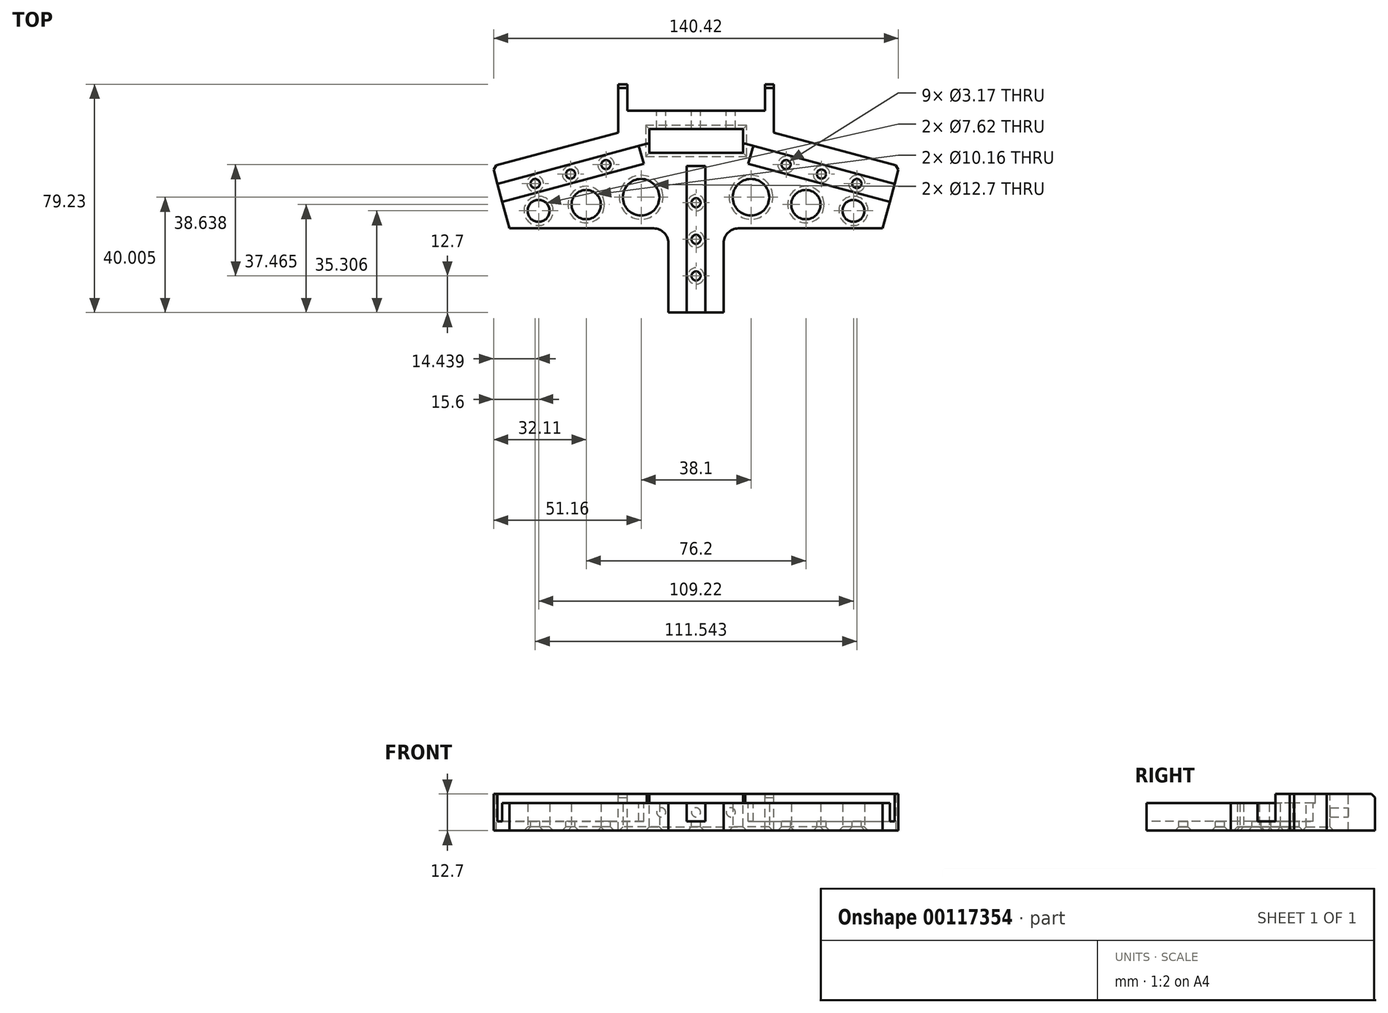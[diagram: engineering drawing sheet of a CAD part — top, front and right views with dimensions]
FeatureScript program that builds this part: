
annotation { "Feature Type Name" : "Feature", "Feature Type Description" : "" }
export const myFeature = defineFeature(function(context is Context, id is Id, definition is map)
    precondition{}
    {
        {
            var Q0;
            Q0=qCreatedBy(makeId("Top.planeOp"),FACE);
            var sketch = newSketch(context, id + "F0", { "sketchPlane" : qUnion([Q0])});
            skLineSegment(sketch, "E0", {"start": v(-70.54, 0) * mm, "end": v(70.54, 0) * mm});
            skLineSegment(sketch, "E1", {"start": v(70.54, 0) * mm, "end": v(0, 18.9) * mm});
            skLineSegment(sketch, "E2", {"start": v(0, 18.9) * mm, "end": v(-70.54, 0) * mm});
            skLineSegment(sketch, "E3", {"start": v(-70.54, 0) * mm, "end": v(-56.92, -50.8) * mm});
            skLineSegment(sketch, "E4", {"start": v(70.54, 0) * mm, "end": v(56.92, -50.8) * mm});
            skPoint(sketch, "E5.orphan", {"position": v(0, -50.8) * mm});
            skLineSegment(sketch, "E6", {"start": v(-56.92, -50.8) * mm, "end": v(56.92, -50.8) * mm});
            skSolve(sketch);
        }
        {
            var Q0;
            Q0=qSketchRegion(id+"F0",true);
            extrude(context, id + "F1", {"entities" : qUnion([Q0]), "depth" : 9.52 * mm});
        }
        {
            var Q0;
            Q0=makeQuery(id+"F1.opExtrude","CAP_FACE",FACE,{"disambiguationData":[OSD([sQuery(id+"F0.wireOp",EDGE,"E1"),sQuery(id+"F0.wireOp",EDGE,"E2"),sQuery(id+"F0.wireOp",EDGE,"E3"),sQuery(id+"F0.wireOp",EDGE,"E4"),sQuery(id+"F0.wireOp",EDGE,"E6")])],"isStart":false});
            var sketch = newSketch(context, id + "F2", { "sketchPlane" : qUnion([Q0])});
            skLineSegment(sketch, "E7", {"start": v(-70.54, 0) * mm, "end": v(0, 18.9) * mm});
            skLineSegment(sketch, "E8", {"start": v(0, 18.9) * mm, "end": v(70.54, 0) * mm});
            skLineSegment(sketch, "E9", {"start": v(70.54, 0) * mm, "end": v(68.9, -6.13) * mm});
            skLineSegment(sketch, "E10", {"start": v(68.9, -6.13) * mm, "end": v(0, 12.33) * mm});
            skLineSegment(sketch, "E11", {"start": v(0, 12.33) * mm, "end": v(-68.9, -6.13) * mm});
            skLineSegment(sketch, "E12", {"start": v(-68.9, -6.13) * mm, "end": v(-70.54, 0) * mm});
            skSolve(sketch);
        }
        {
            var Q0;
            Q0=qSketchRegion(id+"F2",true);
            extrude(context, id + "F3", {"entities" : qUnion([Q0]), "operationType" : NewBodyOperationType.ADD, "endBound" : BoundingType.SYMMETRIC, "depth" : 6.35 * mm});
        }
        {
            var Q0;
            Q0=makeQuery(id+"F1.opExtrude","CAP_FACE",FACE,{"disambiguationData":[OSD([sQuery(id+"F0.wireOp",EDGE,"E1"),sQuery(id+"F0.wireOp",EDGE,"E2"),sQuery(id+"F0.wireOp",EDGE,"E3"),sQuery(id+"F0.wireOp",EDGE,"E4"),sQuery(id+"F0.wireOp",EDGE,"E6")])],"isStart":false});
            var sketch = newSketch(context, id + "F4", { "sketchPlane" : qUnion([Q0])});
            skLineSegment(sketch, "E13", {"start": v(-3.24, 0) * mm, "end": v(-3.24, -50.8) * mm});
            skLineSegment(sketch, "E14", {"start": v(-3.24, -50.8) * mm, "end": v(3.24, -50.8) * mm});
            skLineSegment(sketch, "E15", {"start": v(3.24, -50.8) * mm, "end": v(3.24, 0) * mm});
            skLineSegment(sketch, "E16", {"start": v(3.24, 0) * mm, "end": v(-3.24, 0) * mm});
            skSolve(sketch);
        }
        {
            var Q0;
            Q0=qSketchRegion(id+"F4",true);
            extrude(context, id + "F5", {"entities" : qUnion([Q0]), "operationType" : NewBodyOperationType.REMOVE, "oppositeDirection" : true, "depth" : 6.35 * mm});
        }
        {
            var Q0;
            {var subQ0=sQuery(id+"F0.wireOp",EDGE,"E6");var subQ1=sQuery(id+"F0.wireOp",EDGE,"E3");var subQ2=makeQuery(id+"F1.opExtrude","CAP_FACE",FACE,{"disambiguationData":[OSD([sQuery(id+"F0.wireOp",EDGE,"E1"),sQuery(id+"F0.wireOp",EDGE,"E2"),subQ1,sQuery(id+"F0.wireOp",EDGE,"E4"),subQ0])],"isStart":false});Q0=makeQuery(id+"F5.boolean.opBoolean","SPLIT",FACE,{"disambiguationData":[TD([subQ2,makeQuery(id+"F1.opExtrude","SWEPT_FACE",FACE,{"disambiguationData":[OSD([subQ1])]}),makeQuery(id+"F1.opExtrude","SWEPT_FACE",FACE,{"disambiguationData":[OSD([subQ0])]}),makeQuery(id+"F3.opExtrude","SWEPT_FACE",FACE,{"disambiguationData":[OSD([sQuery(id+"F2.wireOp",EDGE,"E11")])]}),makeQuery(id+"F3.opExtrude","SWEPT_FACE",FACE,{"disambiguationData":[OSD([sQuery(id+"F2.wireOp",EDGE,"E12")])]}),makeQuery(id+"F5.opExtrude","SWEPT_FACE",FACE,{"disambiguationData":[OSD([sQuery(id+"F4.wireOp",EDGE,"E13")])]}),makeQuery(id+"F5.opExtrude","SWEPT_FACE",FACE,{"disambiguationData":[OSD([sQuery(id+"F4.wireOp",EDGE,"E16")])]})])],"derivedFrom":subQ2});}
            var sketch = newSketch(context, id + "F6", { "sketchPlane" : qUnion([Q0])});
            skLineSegment(sketch, "E17", {"start": v(-67.22, -12.39) * mm, "end": v(-68.9, -6.13) * mm});
            skLineSegment(sketch, "E18", {"start": v(-68.9, -6.13) * mm, "end": v(-19.82, 7.01) * mm});
            skLineSegment(sketch, "E19", {"start": v(-19.82, 7.01) * mm, "end": v(-18.15, 0.76) * mm});
            skLineSegment(sketch, "E20", {"start": v(-18.15, 0.76) * mm, "end": v(-67.22, -12.39) * mm});
            skLineSegment(sketch, "E21", {"start": v(0, 11.92) * mm, "end": v(0, -51.16) * mm});
            skLineSegment(sketch, "E22.MirrorCS", {"start": v(68.9, -6.13) * mm, "end": v(19.82, 7.01) * mm});
            skLineSegment(sketch, "E23.MirrorCS", {"start": v(18.15, 0.76) * mm, "end": v(67.22, -12.39) * mm});
            skLineSegment(sketch, "E24.MirrorCS", {"start": v(67.22, -12.39) * mm, "end": v(68.9, -6.13) * mm});
            skLineSegment(sketch, "E25.MirrorCS", {"start": v(19.82, 7.01) * mm, "end": v(18.15, 0.76) * mm});
            skSolve(sketch);
        }
        {
            var Q0;
            Q0=qSketchRegion(id+"F6",true);
            extrude(context, id + "F7", {"entities" : qUnion([Q0]), "operationType" : NewBodyOperationType.REMOVE, "oppositeDirection" : true, "depth" : 6.35 * mm});
        }
        {
            var Q0;
            Q0=makeQuery(id+"F5.boolean.opBoolean","COPY",FACE,{"derivedFrom":makeQuery(id+"F5.opExtrude","CAP_FACE",FACE,{"disambiguationData":[OSD([sQuery(id+"F4.wireOp",EDGE,"E13"),sQuery(id+"F4.wireOp",EDGE,"E14"),sQuery(id+"F4.wireOp",EDGE,"E15"),sQuery(id+"F4.wireOp",EDGE,"E16")])],"isStart":false})});
            var sketch = newSketch(context, id + "F8", { "sketchPlane" : qUnion([Q0])});
            skLineSegment(sketch, "E26", {"start": v(0, 0) * mm, "end": v(0, -50.8) * mm});
            skSolve(sketch);
        }
        {
            var Q0;
            Q0=makeQuery(id+"F7.boolean.opBoolean","COPY",FACE,{"derivedFrom":makeQuery(id+"F7.opExtrude","CAP_FACE",FACE,{"disambiguationData":[OSD([sQuery(id+"F6.wireOp",EDGE,"E17"),sQuery(id+"F6.wireOp",EDGE,"E18"),sQuery(id+"F6.wireOp",EDGE,"E19"),sQuery(id+"F6.wireOp",EDGE,"E20")])],"isStart":false})});
            var sketch = newSketch(context, id + "F9", { "sketchPlane" : qUnion([Q0])});
            skCircle(sketch, "E27", {"center": v(-55.77, -6.04) * mm, "radius": 1.59 * mm});
            skCircle(sketch, "E28", {"center": v(-43.5, -2.75) * mm, "radius": 1.59 * mm});
            skCircle(sketch, "E29", {"center": v(-31.24, 0.54) * mm, "radius": 1.59 * mm});
            skCircle(sketch, "E30.MirrorC", {"center": v(31.24, 0.54) * mm, "radius": 1.59 * mm});
            skCircle(sketch, "E31.MirrorC", {"center": v(43.5, -2.75) * mm, "radius": 1.59 * mm});
            skCircle(sketch, "E32.MirrorC", {"center": v(55.77, -6.04) * mm, "radius": 1.59 * mm});
            skCircle(sketch, "E33", {"center": v(0, -12.7) * mm, "radius": 1.59 * mm});
            skCircle(sketch, "E34", {"center": v(0, -25.4) * mm, "radius": 1.59 * mm});
            skCircle(sketch, "E35", {"center": v(0, -38.1) * mm, "radius": 1.59 * mm});
            skSolve(sketch);
        }
        {
            var Q0;
            Q0=qSketchRegion(id+"F9",true);
            extrude(context, id + "F10", {"entities" : qUnion([Q0]), "operationType" : NewBodyOperationType.REMOVE, "oppositeDirection" : true, "depth" : 25.4 * mm});
        }
        {
            var Q0;
            {var subQ0=sQuery(id+"F0.wireOp",EDGE,"E6");var subQ1=sQuery(id+"F0.wireOp",EDGE,"E3");var subQ2=makeQuery(id+"F1.opExtrude","CAP_FACE",FACE,{"disambiguationData":[OSD([sQuery(id+"F0.wireOp",EDGE,"E1"),sQuery(id+"F0.wireOp",EDGE,"E2"),subQ1,sQuery(id+"F0.wireOp",EDGE,"E4"),subQ0])],"isStart":false});Q0=makeQuery(id+"F5.boolean.opBoolean","SPLIT",FACE,{"disambiguationData":[TD([subQ2,makeQuery(id+"F1.opExtrude","SWEPT_FACE",FACE,{"disambiguationData":[OSD([subQ1])]}),makeQuery(id+"F1.opExtrude","SWEPT_FACE",FACE,{"disambiguationData":[OSD([subQ0])]}),makeQuery(id+"F3.opExtrude","SWEPT_FACE",FACE,{"disambiguationData":[OSD([sQuery(id+"F2.wireOp",EDGE,"E11")])]}),makeQuery(id+"F3.opExtrude","SWEPT_FACE",FACE,{"disambiguationData":[OSD([sQuery(id+"F2.wireOp",EDGE,"E12")])]}),makeQuery(id+"F5.opExtrude","SWEPT_FACE",FACE,{"disambiguationData":[OSD([sQuery(id+"F4.wireOp",EDGE,"E13")])]}),makeQuery(id+"F5.opExtrude","SWEPT_FACE",FACE,{"disambiguationData":[OSD([sQuery(id+"F4.wireOp",EDGE,"E16")])]})])],"derivedFrom":subQ2});}
            var sketch = newSketch(context, id + "F11", { "sketchPlane" : qUnion([Q0])});
            skLineSegment(sketch, "E36", {"start": v(-56.92, -50.8) * mm, "end": v(-9.59, -50.8) * mm});
            skLineSegment(sketch, "E37", {"start": v(-9.59, -50.8) * mm, "end": v(-9.59, -21.6) * mm});
            skLineSegment(sketch, "E38", {"start": v(-9.59, -21.6) * mm, "end": v(-64.75, -21.6) * mm});
            skLineSegment(sketch, "E39", {"start": v(-64.75, -21.6) * mm, "end": v(-56.92, -50.8) * mm});
            skLineSegment(sketch, "E40", {"start": v(0, 0) * mm, "end": v(0, -52.9) * mm});
            skLineSegment(sketch, "E41.MirrorCS", {"start": v(64.75, -21.6) * mm, "end": v(56.92, -50.8) * mm});
            skLineSegment(sketch, "E42.MirrorCS", {"start": v(56.92, -50.8) * mm, "end": v(9.59, -50.8) * mm});
            skLineSegment(sketch, "E43.MirrorCS", {"start": v(9.59, -21.6) * mm, "end": v(64.75, -21.6) * mm});
            skLineSegment(sketch, "E44.MirrorCS", {"start": v(9.59, -50.8) * mm, "end": v(9.59, -21.6) * mm});
            skCircle(sketch, "E45", {"center": v(-19.05, -10.8) * mm, "radius": 6.35 * mm});
            skCircle(sketch, "E46.MirrorC", {"center": v(19.05, -10.8) * mm, "radius": 6.35 * mm});
            skCircle(sketch, "E47", {"center": v(-38.1, -13.34) * mm, "radius": 5.08 * mm});
            skCircle(sketch, "E48", {"center": v(-54.61, -15.5) * mm, "radius": 3.81 * mm});
            skCircle(sketch, "E49.MirrorC", {"center": v(38.1, -13.34) * mm, "radius": 5.08 * mm});
            skCircle(sketch, "E50.MirrorC", {"center": v(54.61, -15.5) * mm, "radius": 3.81 * mm});
            skSolve(sketch);
        }
        {
            var Q0;
            Q0=qSketchRegion(id+"F11",true);
            extrude(context, id + "F12", {"entities" : qUnion([Q0]), "operationType" : NewBodyOperationType.REMOVE, "endBound" : BoundingType.SYMMETRIC, "depth" : 25.4 * mm});
        }
        {
            var Q0;
            Q0=makeQuery(id+"F3.opExtrude","CAP_FACE",FACE,{"disambiguationData":[OSD([sQuery(id+"F2.wireOp",EDGE,"E7"),sQuery(id+"F2.wireOp",EDGE,"E8"),sQuery(id+"F2.wireOp",EDGE,"E9"),sQuery(id+"F2.wireOp",EDGE,"E10"),sQuery(id+"F2.wireOp",EDGE,"E11"),sQuery(id+"F2.wireOp",EDGE,"E12")])],"isStart":false});
            var sketch = newSketch(context, id + "F13", { "sketchPlane" : qUnion([Q0])});
            skLineSegment(sketch, "E51", {"start": v(-26.99, 11.67) * mm, "end": v(-26.99, 28.43) * mm});
            skLineSegment(sketch, "E52", {"start": v(-26.99, 28.43) * mm, "end": v(26.99, 28.43) * mm});
            skLineSegment(sketch, "E53", {"start": v(26.99, 28.43) * mm, "end": v(26.99, 11.67) * mm});
            skLineSegment(sketch, "E54", {"start": v(26.99, 11.67) * mm, "end": v(0, 18.9) * mm});
            skLineSegment(sketch, "E55", {"start": v(0, 18.9) * mm, "end": v(-26.99, 11.67) * mm});
            skSolve(sketch);
        }
        {
            var Q0;
            Q0=makeQuery(id+"F13.imprint","IMPRINT",FACE,{"disambiguationData":[TD([[makeQuery(id+"F13.imprint","IMPRINT",EDGE,{"derivedFrom":sQuery(id+"F13.wireOp",EDGE,"E51")}),-1.0]])]});
            extrude(context, id + "F14", {"entities" : qUnion([Q0]), "operationType" : NewBodyOperationType.ADD, "oppositeDirection" : true, "depth" : 12.7 * mm});
        }
        {
            var Q0;
            Q0=makeQuery(id+"F14.boolean.opBoolean","MERGE",FACE,{"derivedFrom":[makeQuery(id+"F3.opExtrude","CAP_FACE",FACE,{"disambiguationData":[OSD([sQuery(id+"F2.wireOp",EDGE,"E7"),sQuery(id+"F2.wireOp",EDGE,"E8"),sQuery(id+"F2.wireOp",EDGE,"E9"),sQuery(id+"F2.wireOp",EDGE,"E10"),sQuery(id+"F2.wireOp",EDGE,"E11"),sQuery(id+"F2.wireOp",EDGE,"E12")])],"isStart":false}),makeQuery(id+"F14.opExtrude","CAP_FACE",FACE,{"disambiguationData":[OSD([sQuery(id+"F13.wireOp",EDGE,"E51"),sQuery(id+"F13.wireOp",EDGE,"E52"),sQuery(id+"F13.wireOp",EDGE,"E53"),sQuery(id+"F13.wireOp",EDGE,"E54"),sQuery(id+"F13.wireOp",EDGE,"E55")])],"isStart":true})]});
            var sketch = newSketch(context, id + "F15", { "sketchPlane" : qUnion([Q0])});
            skLineSegment(sketch, "E56", {"start": v(-23.81, 28.43) * mm, "end": v(-23.81, 19.2) * mm});
            skLineSegment(sketch, "E57", {"start": v(-23.81, 19.2) * mm, "end": v(23.94, 19.2) * mm});
            skLineSegment(sketch, "E58", {"start": v(23.94, 19.2) * mm, "end": v(23.94, 28.43) * mm});
            skLineSegment(sketch, "E59", {"start": v(23.94, 28.43) * mm, "end": v(-23.81, 28.43) * mm});
            skSolve(sketch);
        }
        {
            var Q0;
            Q0=qSketchRegion(id+"F15",true);
            extrude(context, id + "F16", {"entities" : qUnion([Q0]), "operationType" : NewBodyOperationType.REMOVE, "oppositeDirection" : true, "depth" : 25.4 * mm});
        }
        {
            var Q0;
            Q0=makeQuery(id+"F14.boolean.opBoolean","MERGE",FACE,{"derivedFrom":[makeQuery(id+"F3.opExtrude","CAP_FACE",FACE,{"disambiguationData":[OSD([sQuery(id+"F2.wireOp",EDGE,"E7"),sQuery(id+"F2.wireOp",EDGE,"E8"),sQuery(id+"F2.wireOp",EDGE,"E9"),sQuery(id+"F2.wireOp",EDGE,"E10"),sQuery(id+"F2.wireOp",EDGE,"E11"),sQuery(id+"F2.wireOp",EDGE,"E12")])],"isStart":false}),makeQuery(id+"F14.opExtrude","CAP_FACE",FACE,{"disambiguationData":[OSD([sQuery(id+"F13.wireOp",EDGE,"E51"),sQuery(id+"F13.wireOp",EDGE,"E52"),sQuery(id+"F13.wireOp",EDGE,"E53"),sQuery(id+"F13.wireOp",EDGE,"E54"),sQuery(id+"F13.wireOp",EDGE,"E55")])],"isStart":true})]});
            var sketch = newSketch(context, id + "F17", { "sketchPlane" : qUnion([Q0])});
            skLineSegment(sketch, "E60", {"start": v(-17.05, 7.76) * mm, "end": v(17.05, 7.76) * mm});
            skLineSegment(sketch, "E61", {"start": v(17.05, 7.76) * mm, "end": v(0, 12.33) * mm});
            skLineSegment(sketch, "E62", {"start": v(0, 12.33) * mm, "end": v(-17.05, 7.76) * mm});
            skSolve(sketch);
        }
        {
            var Q0;
            Q0=qSketchRegion(id+"F17",true);
            extrude(context, id + "F18", {"entities" : qUnion([Q0]), "operationType" : NewBodyOperationType.ADD, "oppositeDirection" : true, "depth" : 12.7 * mm});
        }
        {
            var Q0;
            Q0=makeQuery(id+"F18.boolean.opBoolean","MERGE",FACE,{"derivedFrom":[makeQuery(id+"F14.boolean.opBoolean","MERGE",FACE,{"derivedFrom":[makeQuery(id+"F3.opExtrude","CAP_FACE",FACE,{"disambiguationData":[OSD([sQuery(id+"F2.wireOp",EDGE,"E7"),sQuery(id+"F2.wireOp",EDGE,"E8"),sQuery(id+"F2.wireOp",EDGE,"E9"),sQuery(id+"F2.wireOp",EDGE,"E10"),sQuery(id+"F2.wireOp",EDGE,"E11"),sQuery(id+"F2.wireOp",EDGE,"E12")])],"isStart":false}),makeQuery(id+"F14.opExtrude","CAP_FACE",FACE,{"disambiguationData":[OSD([sQuery(id+"F13.wireOp",EDGE,"E51"),sQuery(id+"F13.wireOp",EDGE,"E52"),sQuery(id+"F13.wireOp",EDGE,"E53"),sQuery(id+"F13.wireOp",EDGE,"E54"),sQuery(id+"F13.wireOp",EDGE,"E55")])],"isStart":true})]}),makeQuery(id+"F18.opExtrude","CAP_FACE",FACE,{"disambiguationData":[OSD([sQuery(id+"F17.wireOp",EDGE,"E60"),sQuery(id+"F17.wireOp",EDGE,"E61"),sQuery(id+"F17.wireOp",EDGE,"E62")])],"isStart":true})]});
            var sketch = newSketch(context, id + "F19", { "sketchPlane" : qUnion([Q0])});
            skLineSegment(sketch, "E63", {"start": v(-16.2, 12.86) * mm, "end": v(-16.2, 7.76) * mm});
            skLineSegment(sketch, "E64", {"start": v(-16.2, 7.76) * mm, "end": v(16.32, 7.76) * mm});
            skLineSegment(sketch, "E65", {"start": v(16.32, 7.76) * mm, "end": v(16.32, 12.86) * mm});
            skLineSegment(sketch, "E66", {"start": v(16.32, 12.86) * mm, "end": v(-16.2, 12.86) * mm});
            skSolve(sketch);
        }
        {
            var Q0;
            Q0=qSketchRegion(id+"F19",true);
            extrude(context, id + "F20", {"entities" : qUnion([Q0]), "operationType" : NewBodyOperationType.REMOVE, "oppositeDirection" : true, "depth" : 25.4 * mm});
        }
        {
            var Q0;
            Q0=makeQuery(id+"F1.opExtrude","CAP_FACE",FACE,{"disambiguationData":[OSD([sQuery(id+"F0.wireOp",EDGE,"E1"),sQuery(id+"F0.wireOp",EDGE,"E2"),sQuery(id+"F0.wireOp",EDGE,"E3"),sQuery(id+"F0.wireOp",EDGE,"E4"),sQuery(id+"F0.wireOp",EDGE,"E6")])],"isStart":false});
            var sketch = newSketch(context, id + "F21", { "sketchPlane" : qUnion([Q0])});
            skLineSegment(sketch, "E67", {"start": v(-16.2, 7.76) * mm, "end": v(-16.2, 4.58) * mm});
            skLineSegment(sketch, "E68", {"start": v(-16.2, 4.58) * mm, "end": v(16.32, 4.58) * mm});
            skLineSegment(sketch, "E69", {"start": v(16.32, 4.58) * mm, "end": v(16.32, 7.76) * mm});
            skLineSegment(sketch, "E70", {"start": v(16.32, 7.76) * mm, "end": v(-16.2, 7.76) * mm});
            skSolve(sketch);
        }
        {
            var Q0;
            Q0=qSketchRegion(id+"F21",true);
            extrude(context, id + "F22", {"entities" : qUnion([Q0]), "operationType" : NewBodyOperationType.REMOVE, "oppositeDirection" : true, "depth" : 25.4 * mm});
        }
        {
            var Q0;
            Q0=makeQuery(id+"F16.boolean.opBoolean","COPY",FACE,{"derivedFrom":makeQuery(id+"F16.opExtrude","SWEPT_FACE",FACE,{"disambiguationData":[OSD([sQuery(id+"F15.wireOp",EDGE,"E57")])]})});
            var sketch = newSketch(context, id + "F23", { "sketchPlane" : qUnion([Q0])});
            skCircle(sketch, "E71", {"center": v(0, 6.35) * mm, "radius": 1.59 * mm});
            skCircle(sketch, "E72", {"center": v(-12.07, 6.35) * mm, "radius": 1.59 * mm});
            skCircle(sketch, "E73", {"center": v(12.07, 6.35) * mm, "radius": 1.59 * mm});
            skSolve(sketch);
        }
        {
            var Q0;
            Q0=qSketchRegion(id+"F23",true);
            extrude(context, id + "F24", {"entities" : qUnion([Q0]), "operationType" : NewBodyOperationType.REMOVE, "oppositeDirection" : true, "depth" : 8.9 * mm});
        }
        {
            var Q0;
            Q0=makeQuery(id+"F14.opExtrude","SWEPT_EDGE",EDGE,{"disambiguationData":[OSD([sQuery(id+"F2.wireOp",EDGE,"E7"),sQuery(id+"F13.wireOp",EDGE,"E51"),sQuery(id+"F13.wireOp",EDGE,"E55")])]});
            var Q1;
            Q1=makeQuery(id+"F14.opExtrude","SWEPT_EDGE",EDGE,{"disambiguationData":[OSD([sQuery(id+"F2.wireOp",EDGE,"E8"),sQuery(id+"F13.wireOp",EDGE,"E53"),sQuery(id+"F13.wireOp",EDGE,"E54")])]});
            var Q2;
            Q2=makeQuery(id+"F12.boolean.opBoolean","COPY",EDGE,{"derivedFrom":makeQuery(id+"F12.opExtrude","SWEPT_EDGE",EDGE,{"disambiguationData":[OSD([sQuery(id+"F11.wireOp",EDGE,"E43.MirrorCS"),sQuery(id+"F11.wireOp",EDGE,"E44.MirrorCS")])]})});
            var Q3;
            Q3=makeQuery(id+"F12.boolean.opBoolean","COPY",EDGE,{"derivedFrom":makeQuery(id+"F12.opExtrude","SWEPT_EDGE",EDGE,{"disambiguationData":[OSD([sQuery(id+"F11.wireOp",EDGE,"E37"),sQuery(id+"F11.wireOp",EDGE,"E38")])]})});
            fillet(context, id + "F25", {"entities" : qUnion([Q0, Q1, Q2, Q3]), "radius" : 5.08 * mm, "tangentPropagation" : true, "allowEdgeOverflow" : false});
        }
        {
            var Q0;
            Q0=makeQuery(id+"F5.boolean.opBoolean","COPY",EDGE,{"derivedFrom":makeQuery(id+"F5.opExtrude","CAP_EDGE",EDGE,{"disambiguationData":[OSD([sQuery(id+"F4.wireOp",EDGE,"E15")])],"isStart":true})});
            var Q1;
            Q1=makeQuery(id+"F5.boolean.opBoolean","COPY",EDGE,{"derivedFrom":makeQuery(id+"F5.opExtrude","CAP_EDGE",EDGE,{"disambiguationData":[OSD([sQuery(id+"F4.wireOp",EDGE,"E13")])],"isStart":true})});
            var Q2;
            Q2=makeQuery(id+"F7.boolean.opBoolean","COPY",EDGE,{"derivedFrom":makeQuery(id+"F7.opExtrude","CAP_EDGE",EDGE,{"disambiguationData":[OSD([sQuery(id+"F6.wireOp",EDGE,"E23.MirrorCS")])],"isStart":true})});
            var Q3;
            Q3=makeQuery(id+"F7.boolean.opBoolean","COPY",EDGE,{"derivedFrom":makeQuery(id+"F7.opExtrude","CAP_EDGE",EDGE,{"disambiguationData":[OSD([sQuery(id+"F6.wireOp",EDGE,"E20")])],"isStart":true})});
            var Q4;
            {var subQ0=sQuery(id+"F13.wireOp",EDGE,"E52");var subQ1=sQuery(id+"F13.wireOp",EDGE,"E53");Q4=makeQuery(id+"F16.boolean.opBoolean","SPLIT",EDGE,{"disambiguationData":[TD([makeQuery(id+"F14.opExtrude","SWEPT_FACE",FACE,{"disambiguationData":[OSD([subQ1])]})])],"derivedFrom":makeQuery(id+"F14.opExtrude","CAP_EDGE",EDGE,{"disambiguationData":[OSD([subQ0])],"isStart":true})});}
            var Q5;
            {var subQ0=sQuery(id+"F13.wireOp",EDGE,"E52");var subQ1=sQuery(id+"F13.wireOp",EDGE,"E51");Q5=makeQuery(id+"F16.boolean.opBoolean","SPLIT",EDGE,{"disambiguationData":[TD([makeQuery(id+"F14.opExtrude","SWEPT_FACE",FACE,{"disambiguationData":[OSD([subQ1])]})])],"derivedFrom":makeQuery(id+"F14.opExtrude","CAP_EDGE",EDGE,{"disambiguationData":[OSD([subQ0])],"isStart":true})});}
            var Q6;
            Q6=makeQuery(id+"F3.boolean.opBoolean","MERGE",EDGE,{"derivedFrom":[makeQuery(id+"F1.opExtrude","SWEPT_EDGE",EDGE,{"disambiguationData":[OSD([sQuery(id+"F0.wireOp",EDGE,"E0"),sQuery(id+"F0.wireOp",EDGE,"E1"),sQuery(id+"F0.wireOp",EDGE,"E4")])]}),makeQuery(id+"F3.opExtrude","SWEPT_EDGE",EDGE,{"disambiguationData":[OSD([sQuery(id+"F2.wireOp",EDGE,"E8"),sQuery(id+"F2.wireOp",EDGE,"E9")])]})]});
            var Q7;
            Q7=makeQuery(id+"F3.boolean.opBoolean","MERGE",EDGE,{"derivedFrom":[makeQuery(id+"F1.opExtrude","SWEPT_EDGE",EDGE,{"disambiguationData":[OSD([sQuery(id+"F0.wireOp",EDGE,"E0"),sQuery(id+"F0.wireOp",EDGE,"E2"),sQuery(id+"F0.wireOp",EDGE,"E3")])]}),makeQuery(id+"F3.opExtrude","SWEPT_EDGE",EDGE,{"disambiguationData":[OSD([sQuery(id+"F2.wireOp",EDGE,"E7"),sQuery(id+"F2.wireOp",EDGE,"E12")])]})]});
            var Q8;
            Q8=makeQuery(id+"F12.boolean.opBoolean","COPY",EDGE,{"derivedFrom":makeQuery(id+"F12.opExtrude","SWEPT_EDGE",EDGE,{"disambiguationData":[OSD([sQuery(id+"F0.wireOp",EDGE,"E4"),sQuery(id+"F11.wireOp",EDGE,"E41.MirrorCS"),sQuery(id+"F11.wireOp",EDGE,"E43.MirrorCS")])]})});
            var Q9;
            Q9=makeQuery(id+"F12.boolean.opBoolean","COPY",EDGE,{"derivedFrom":makeQuery(id+"F12.opExtrude","SWEPT_EDGE",EDGE,{"disambiguationData":[OSD([sQuery(id+"F0.wireOp",EDGE,"E6"),sQuery(id+"F11.wireOp",EDGE,"E42.MirrorCS"),sQuery(id+"F11.wireOp",EDGE,"E44.MirrorCS")])]})});
            var Q10;
            Q10=makeQuery(id+"F12.boolean.opBoolean","COPY",EDGE,{"derivedFrom":makeQuery(id+"F12.opExtrude","SWEPT_EDGE",EDGE,{"disambiguationData":[OSD([sQuery(id+"F0.wireOp",EDGE,"E6"),sQuery(id+"F11.wireOp",EDGE,"E36"),sQuery(id+"F11.wireOp",EDGE,"E37")])]})});
            var Q11;
            Q11=makeQuery(id+"F12.boolean.opBoolean","COPY",EDGE,{"derivedFrom":makeQuery(id+"F12.opExtrude","SWEPT_EDGE",EDGE,{"disambiguationData":[OSD([sQuery(id+"F0.wireOp",EDGE,"E3"),sQuery(id+"F11.wireOp",EDGE,"E38"),sQuery(id+"F11.wireOp",EDGE,"E39")])]})});
            var Q12;
            Q12=makeQuery(id+"F12.boolean.opBoolean","INTERSECT",EDGE,{"derivedFrom":[makeQuery(id+"F1.opExtrude","CAP_FACE",FACE,{"disambiguationData":[OSD([sQuery(id+"F0.wireOp",EDGE,"E1"),sQuery(id+"F0.wireOp",EDGE,"E2"),sQuery(id+"F0.wireOp",EDGE,"E3"),sQuery(id+"F0.wireOp",EDGE,"E4"),sQuery(id+"F0.wireOp",EDGE,"E6")])],"isStart":true}),makeQuery(id+"F12.opExtrude","SWEPT_FACE",FACE,{"disambiguationData":[OSD([sQuery(id+"F11.wireOp",EDGE,"E45")])]})]});
            var Q13;
            Q13=makeQuery(id+"F10.boolean.opBoolean","INTERSECT",EDGE,{"derivedFrom":[makeQuery(id+"F1.opExtrude","CAP_FACE",FACE,{"disambiguationData":[OSD([sQuery(id+"F0.wireOp",EDGE,"E1"),sQuery(id+"F0.wireOp",EDGE,"E2"),sQuery(id+"F0.wireOp",EDGE,"E3"),sQuery(id+"F0.wireOp",EDGE,"E4"),sQuery(id+"F0.wireOp",EDGE,"E6")])],"isStart":true}),makeQuery(id+"F10.opExtrude","SWEPT_FACE",FACE,{"disambiguationData":[OSD([sQuery(id+"F9.wireOp",EDGE,"E35")])]})]});
            var Q14;
            Q14=makeQuery(id+"F10.boolean.opBoolean","INTERSECT",EDGE,{"derivedFrom":[makeQuery(id+"F1.opExtrude","CAP_FACE",FACE,{"disambiguationData":[OSD([sQuery(id+"F0.wireOp",EDGE,"E1"),sQuery(id+"F0.wireOp",EDGE,"E2"),sQuery(id+"F0.wireOp",EDGE,"E3"),sQuery(id+"F0.wireOp",EDGE,"E4"),sQuery(id+"F0.wireOp",EDGE,"E6")])],"isStart":true}),makeQuery(id+"F10.opExtrude","SWEPT_FACE",FACE,{"disambiguationData":[OSD([sQuery(id+"F9.wireOp",EDGE,"E34")])]})]});
            var Q15;
            Q15=makeQuery(id+"F10.boolean.opBoolean","INTERSECT",EDGE,{"derivedFrom":[makeQuery(id+"F1.opExtrude","CAP_FACE",FACE,{"disambiguationData":[OSD([sQuery(id+"F0.wireOp",EDGE,"E1"),sQuery(id+"F0.wireOp",EDGE,"E2"),sQuery(id+"F0.wireOp",EDGE,"E3"),sQuery(id+"F0.wireOp",EDGE,"E4"),sQuery(id+"F0.wireOp",EDGE,"E6")])],"isStart":true}),makeQuery(id+"F10.opExtrude","SWEPT_FACE",FACE,{"disambiguationData":[OSD([sQuery(id+"F9.wireOp",EDGE,"E33")])]})]});
            var Q16;
            Q16=makeQuery(id+"F12.boolean.opBoolean","INTERSECT",EDGE,{"derivedFrom":[makeQuery(id+"F1.opExtrude","CAP_FACE",FACE,{"disambiguationData":[OSD([sQuery(id+"F0.wireOp",EDGE,"E1"),sQuery(id+"F0.wireOp",EDGE,"E2"),sQuery(id+"F0.wireOp",EDGE,"E3"),sQuery(id+"F0.wireOp",EDGE,"E4"),sQuery(id+"F0.wireOp",EDGE,"E6")])],"isStart":true}),makeQuery(id+"F12.opExtrude","SWEPT_FACE",FACE,{"disambiguationData":[OSD([sQuery(id+"F11.wireOp",EDGE,"E46.MirrorC")])]})]});
            var Q17;
            Q17=makeQuery(id+"F10.boolean.opBoolean","INTERSECT",EDGE,{"derivedFrom":[makeQuery(id+"F1.opExtrude","CAP_FACE",FACE,{"disambiguationData":[OSD([sQuery(id+"F0.wireOp",EDGE,"E1"),sQuery(id+"F0.wireOp",EDGE,"E2"),sQuery(id+"F0.wireOp",EDGE,"E3"),sQuery(id+"F0.wireOp",EDGE,"E4"),sQuery(id+"F0.wireOp",EDGE,"E6")])],"isStart":true}),makeQuery(id+"F10.opExtrude","SWEPT_FACE",FACE,{"disambiguationData":[OSD([sQuery(id+"F9.wireOp",EDGE,"E30.MirrorC")])]})]});
            var Q18;
            Q18=makeQuery(id+"F10.boolean.opBoolean","INTERSECT",EDGE,{"derivedFrom":[makeQuery(id+"F1.opExtrude","CAP_FACE",FACE,{"disambiguationData":[OSD([sQuery(id+"F0.wireOp",EDGE,"E1"),sQuery(id+"F0.wireOp",EDGE,"E2"),sQuery(id+"F0.wireOp",EDGE,"E3"),sQuery(id+"F0.wireOp",EDGE,"E4"),sQuery(id+"F0.wireOp",EDGE,"E6")])],"isStart":true}),makeQuery(id+"F10.opExtrude","SWEPT_FACE",FACE,{"disambiguationData":[OSD([sQuery(id+"F9.wireOp",EDGE,"E31.MirrorC")])]})]});
            var Q19;
            Q19=makeQuery(id+"F10.boolean.opBoolean","INTERSECT",EDGE,{"derivedFrom":[makeQuery(id+"F1.opExtrude","CAP_FACE",FACE,{"disambiguationData":[OSD([sQuery(id+"F0.wireOp",EDGE,"E1"),sQuery(id+"F0.wireOp",EDGE,"E2"),sQuery(id+"F0.wireOp",EDGE,"E3"),sQuery(id+"F0.wireOp",EDGE,"E4"),sQuery(id+"F0.wireOp",EDGE,"E6")])],"isStart":true}),makeQuery(id+"F10.opExtrude","SWEPT_FACE",FACE,{"disambiguationData":[OSD([sQuery(id+"F9.wireOp",EDGE,"E32.MirrorC")])]})]});
            var Q20;
            Q20=makeQuery(id+"F10.boolean.opBoolean","INTERSECT",EDGE,{"derivedFrom":[makeQuery(id+"F1.opExtrude","CAP_FACE",FACE,{"disambiguationData":[OSD([sQuery(id+"F0.wireOp",EDGE,"E1"),sQuery(id+"F0.wireOp",EDGE,"E2"),sQuery(id+"F0.wireOp",EDGE,"E3"),sQuery(id+"F0.wireOp",EDGE,"E4"),sQuery(id+"F0.wireOp",EDGE,"E6")])],"isStart":true}),makeQuery(id+"F10.opExtrude","SWEPT_FACE",FACE,{"disambiguationData":[OSD([sQuery(id+"F9.wireOp",EDGE,"E29")])]})]});
            var Q21;
            Q21=makeQuery(id+"F10.boolean.opBoolean","INTERSECT",EDGE,{"derivedFrom":[makeQuery(id+"F1.opExtrude","CAP_FACE",FACE,{"disambiguationData":[OSD([sQuery(id+"F0.wireOp",EDGE,"E1"),sQuery(id+"F0.wireOp",EDGE,"E2"),sQuery(id+"F0.wireOp",EDGE,"E3"),sQuery(id+"F0.wireOp",EDGE,"E4"),sQuery(id+"F0.wireOp",EDGE,"E6")])],"isStart":true}),makeQuery(id+"F10.opExtrude","SWEPT_FACE",FACE,{"disambiguationData":[OSD([sQuery(id+"F9.wireOp",EDGE,"E28")])]})]});
            var Q22;
            Q22=makeQuery(id+"F10.boolean.opBoolean","INTERSECT",EDGE,{"derivedFrom":[makeQuery(id+"F1.opExtrude","CAP_FACE",FACE,{"disambiguationData":[OSD([sQuery(id+"F0.wireOp",EDGE,"E1"),sQuery(id+"F0.wireOp",EDGE,"E2"),sQuery(id+"F0.wireOp",EDGE,"E3"),sQuery(id+"F0.wireOp",EDGE,"E4"),sQuery(id+"F0.wireOp",EDGE,"E6")])],"isStart":true}),makeQuery(id+"F10.opExtrude","SWEPT_FACE",FACE,{"disambiguationData":[OSD([sQuery(id+"F9.wireOp",EDGE,"E27")])]})]});
            var Q23;
            Q23=makeQuery(id+"F22.boolean.opBoolean","INTERSECT",EDGE,{"derivedFrom":[makeQuery(id+"F14.boolean.opBoolean","MERGE",FACE,{"derivedFrom":[makeQuery(id+"F1.opExtrude","CAP_FACE",FACE,{"disambiguationData":[OSD([sQuery(id+"F0.wireOp",EDGE,"E1"),sQuery(id+"F0.wireOp",EDGE,"E2"),sQuery(id+"F0.wireOp",EDGE,"E3"),sQuery(id+"F0.wireOp",EDGE,"E4"),sQuery(id+"F0.wireOp",EDGE,"E6")])],"isStart":true}),makeQuery(id+"F14.opExtrude","CAP_FACE",FACE,{"disambiguationData":[OSD([sQuery(id+"F13.wireOp",EDGE,"E51"),sQuery(id+"F13.wireOp",EDGE,"E52"),sQuery(id+"F13.wireOp",EDGE,"E53"),sQuery(id+"F13.wireOp",EDGE,"E54"),sQuery(id+"F13.wireOp",EDGE,"E55")])],"isStart":false})]}),makeQuery(id+"F22.opExtrude","SWEPT_FACE",FACE,{"disambiguationData":[OSD([sQuery(id+"F21.wireOp",EDGE,"E68")])]})]});
            var Q24;
            Q24=makeQuery(id+"F22.boolean.opBoolean","INTERSECT",EDGE,{"derivedFrom":[makeQuery(id+"F14.boolean.opBoolean","MERGE",FACE,{"derivedFrom":[makeQuery(id+"F1.opExtrude","CAP_FACE",FACE,{"disambiguationData":[OSD([sQuery(id+"F0.wireOp",EDGE,"E1"),sQuery(id+"F0.wireOp",EDGE,"E2"),sQuery(id+"F0.wireOp",EDGE,"E3"),sQuery(id+"F0.wireOp",EDGE,"E4"),sQuery(id+"F0.wireOp",EDGE,"E6")])],"isStart":true}),makeQuery(id+"F14.opExtrude","CAP_FACE",FACE,{"disambiguationData":[OSD([sQuery(id+"F13.wireOp",EDGE,"E51"),sQuery(id+"F13.wireOp",EDGE,"E52"),sQuery(id+"F13.wireOp",EDGE,"E53"),sQuery(id+"F13.wireOp",EDGE,"E54"),sQuery(id+"F13.wireOp",EDGE,"E55")])],"isStart":false})]}),makeQuery(id+"F22.opExtrude","SWEPT_FACE",FACE,{"disambiguationData":[OSD([sQuery(id+"F21.wireOp",EDGE,"E67")])]})]});
            var Q25;
            Q25=makeQuery(id+"F20.boolean.opBoolean","INTERSECT",EDGE,{"derivedFrom":[makeQuery(id+"F14.boolean.opBoolean","MERGE",FACE,{"derivedFrom":[makeQuery(id+"F1.opExtrude","CAP_FACE",FACE,{"disambiguationData":[OSD([sQuery(id+"F0.wireOp",EDGE,"E1"),sQuery(id+"F0.wireOp",EDGE,"E2"),sQuery(id+"F0.wireOp",EDGE,"E3"),sQuery(id+"F0.wireOp",EDGE,"E4"),sQuery(id+"F0.wireOp",EDGE,"E6")])],"isStart":true}),makeQuery(id+"F14.opExtrude","CAP_FACE",FACE,{"disambiguationData":[OSD([sQuery(id+"F13.wireOp",EDGE,"E51"),sQuery(id+"F13.wireOp",EDGE,"E52"),sQuery(id+"F13.wireOp",EDGE,"E53"),sQuery(id+"F13.wireOp",EDGE,"E54"),sQuery(id+"F13.wireOp",EDGE,"E55")])],"isStart":false})]}),makeQuery(id+"F20.opExtrude","SWEPT_FACE",FACE,{"disambiguationData":[OSD([sQuery(id+"F19.wireOp",EDGE,"E66")])]})]});
            var Q26;
            Q26=makeQuery(id+"F22.boolean.opBoolean","INTERSECT",EDGE,{"derivedFrom":[makeQuery(id+"F14.boolean.opBoolean","MERGE",FACE,{"derivedFrom":[makeQuery(id+"F1.opExtrude","CAP_FACE",FACE,{"disambiguationData":[OSD([sQuery(id+"F0.wireOp",EDGE,"E1"),sQuery(id+"F0.wireOp",EDGE,"E2"),sQuery(id+"F0.wireOp",EDGE,"E3"),sQuery(id+"F0.wireOp",EDGE,"E4"),sQuery(id+"F0.wireOp",EDGE,"E6")])],"isStart":true}),makeQuery(id+"F14.opExtrude","CAP_FACE",FACE,{"disambiguationData":[OSD([sQuery(id+"F13.wireOp",EDGE,"E51"),sQuery(id+"F13.wireOp",EDGE,"E52"),sQuery(id+"F13.wireOp",EDGE,"E53"),sQuery(id+"F13.wireOp",EDGE,"E54"),sQuery(id+"F13.wireOp",EDGE,"E55")])],"isStart":false})]}),makeQuery(id+"F22.opExtrude","SWEPT_FACE",FACE,{"disambiguationData":[OSD([sQuery(id+"F21.wireOp",EDGE,"E69")])]})]});
            var Q27;
            Q27=makeQuery(id+"F12.boolean.opBoolean","INTERSECT",EDGE,{"derivedFrom":[makeQuery(id+"F1.opExtrude","CAP_FACE",FACE,{"disambiguationData":[OSD([sQuery(id+"F0.wireOp",EDGE,"E1"),sQuery(id+"F0.wireOp",EDGE,"E2"),sQuery(id+"F0.wireOp",EDGE,"E3"),sQuery(id+"F0.wireOp",EDGE,"E4"),sQuery(id+"F0.wireOp",EDGE,"E6")])],"isStart":true}),makeQuery(id+"F12.opExtrude","SWEPT_FACE",FACE,{"disambiguationData":[OSD([sQuery(id+"F11.wireOp",EDGE,"E50.MirrorC")])]})]});
            var Q28;
            Q28=makeQuery(id+"F12.boolean.opBoolean","INTERSECT",EDGE,{"derivedFrom":[makeQuery(id+"F1.opExtrude","CAP_FACE",FACE,{"disambiguationData":[OSD([sQuery(id+"F0.wireOp",EDGE,"E1"),sQuery(id+"F0.wireOp",EDGE,"E2"),sQuery(id+"F0.wireOp",EDGE,"E3"),sQuery(id+"F0.wireOp",EDGE,"E4"),sQuery(id+"F0.wireOp",EDGE,"E6")])],"isStart":true}),makeQuery(id+"F12.opExtrude","SWEPT_FACE",FACE,{"disambiguationData":[OSD([sQuery(id+"F11.wireOp",EDGE,"E49.MirrorC")])]})]});
            var Q29;
            Q29=makeQuery(id+"F12.boolean.opBoolean","INTERSECT",EDGE,{"derivedFrom":[makeQuery(id+"F1.opExtrude","CAP_FACE",FACE,{"disambiguationData":[OSD([sQuery(id+"F0.wireOp",EDGE,"E1"),sQuery(id+"F0.wireOp",EDGE,"E2"),sQuery(id+"F0.wireOp",EDGE,"E3"),sQuery(id+"F0.wireOp",EDGE,"E4"),sQuery(id+"F0.wireOp",EDGE,"E6")])],"isStart":true}),makeQuery(id+"F12.opExtrude","SWEPT_FACE",FACE,{"disambiguationData":[OSD([sQuery(id+"F11.wireOp",EDGE,"E47")])]})]});
            var Q30;
            Q30=makeQuery(id+"F12.boolean.opBoolean","INTERSECT",EDGE,{"derivedFrom":[makeQuery(id+"F1.opExtrude","CAP_FACE",FACE,{"disambiguationData":[OSD([sQuery(id+"F0.wireOp",EDGE,"E1"),sQuery(id+"F0.wireOp",EDGE,"E2"),sQuery(id+"F0.wireOp",EDGE,"E3"),sQuery(id+"F0.wireOp",EDGE,"E4"),sQuery(id+"F0.wireOp",EDGE,"E6")])],"isStart":true}),makeQuery(id+"F12.opExtrude","SWEPT_FACE",FACE,{"disambiguationData":[OSD([sQuery(id+"F11.wireOp",EDGE,"E48")])]})]});
            chamfer(context, id + "F26", {"entities" : qUnion([Q0, Q1, Q2, Q3, Q4, Q5, Q6, Q7, Q8, Q9, Q10, Q11, Q12, Q13, Q14, Q15, Q16, Q17, Q18, Q19, Q20, Q21, Q22, Q23, Q24, Q25, Q26, Q27, Q28, Q29, Q30]), "width" : 1.27 * mm, "tangentPropagation" : true});
        }
    });
